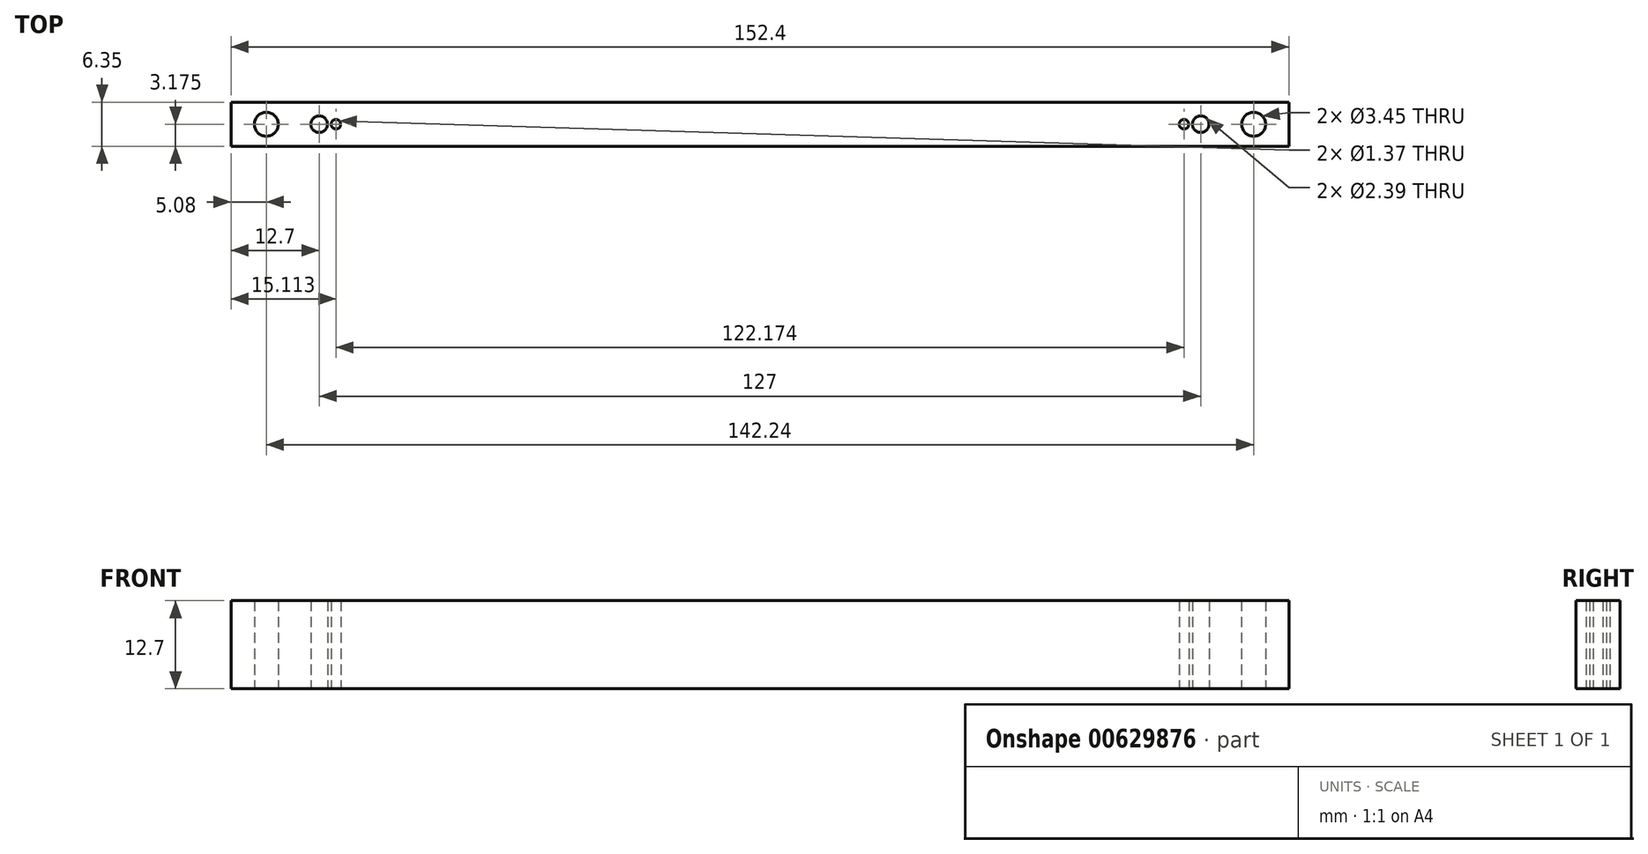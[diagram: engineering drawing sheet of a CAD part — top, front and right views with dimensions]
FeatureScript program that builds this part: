
annotation { "Feature Type Name" : "Feature", "Feature Type Description" : "" }
export const myFeature = defineFeature(function(context is Context, id is Id, definition is map)
    precondition{}
    {
        {
            var Q0;
            Q0=qCreatedBy(makeId("Top.planeOp"),FACE);
            var sketch = newSketch(context, id + "F0", { "sketchPlane" : qUnion([Q0])});
            skLineSegment(sketch, "E0.bottom", {"start": v(0, 0) * mm, "end": v(152.4, 0) * mm});
            skLineSegment(sketch, "E0.top", {"start": v(0, 6.35) * mm, "end": v(152.4, 6.35) * mm});
            skLineSegment(sketch, "E0.left", {"start": v(0, 0) * mm, "end": v(0, 6.35) * mm});
            skLineSegment(sketch, "E0.right", {"start": v(152.4, 0) * mm, "end": v(152.4, 6.35) * mm});
            skLineSegment(sketch, "E1", {"start": v(76.2, 6.35) * mm, "end": v(76.2, -11.63) * mm, "construction": true});
            skPoint(sketch, "E1.endSnap0", {"position": v(76.2, 0) * mm});
            skLineSegment(sketch, "E2", {"start": v(0, 3.18) * mm, "end": v(152.4, 3.18) * mm, "construction": true});
            skCircle(sketch, "E3", {"center": v(12.7, 3.18) * mm, "radius": 1.2 * mm});
            skCircle(sketch, "E4", {"center": v(15.11, 3.18) * mm, "radius": 0.69 * mm});
            skCircle(sketch, "E5.MirrorC", {"center": v(139.7, 3.17) * mm, "radius": 1.2 * mm});
            skCircle(sketch, "E6.MirrorC", {"center": v(137.29, 3.17) * mm, "radius": 0.69 * mm});
            skCircle(sketch, "E7", {"center": v(5.08, 3.18) * mm, "radius": 1.73 * mm});
            skCircle(sketch, "E8.MirrorC", {"center": v(147.32, 3.17) * mm, "radius": 1.73 * mm});
            skSolve(sketch);
        }
        {
            var Q0;
            Q0=makeQuery(id+"F0.imprint","IMPRINT",FACE,{"disambiguationData":[TD([[makeQuery(id+"F0.imprint","IMPRINT",EDGE,{"derivedFrom":sQuery(id+"F0.wireOp",EDGE,"E0.bottom")}),1.0]])]});
            extrude(context, id + "F1", {"entities" : qUnion([Q0]), "depth" : 12.7 * mm, "offsetDistance" : 25.4 * mm});
        }
    });
